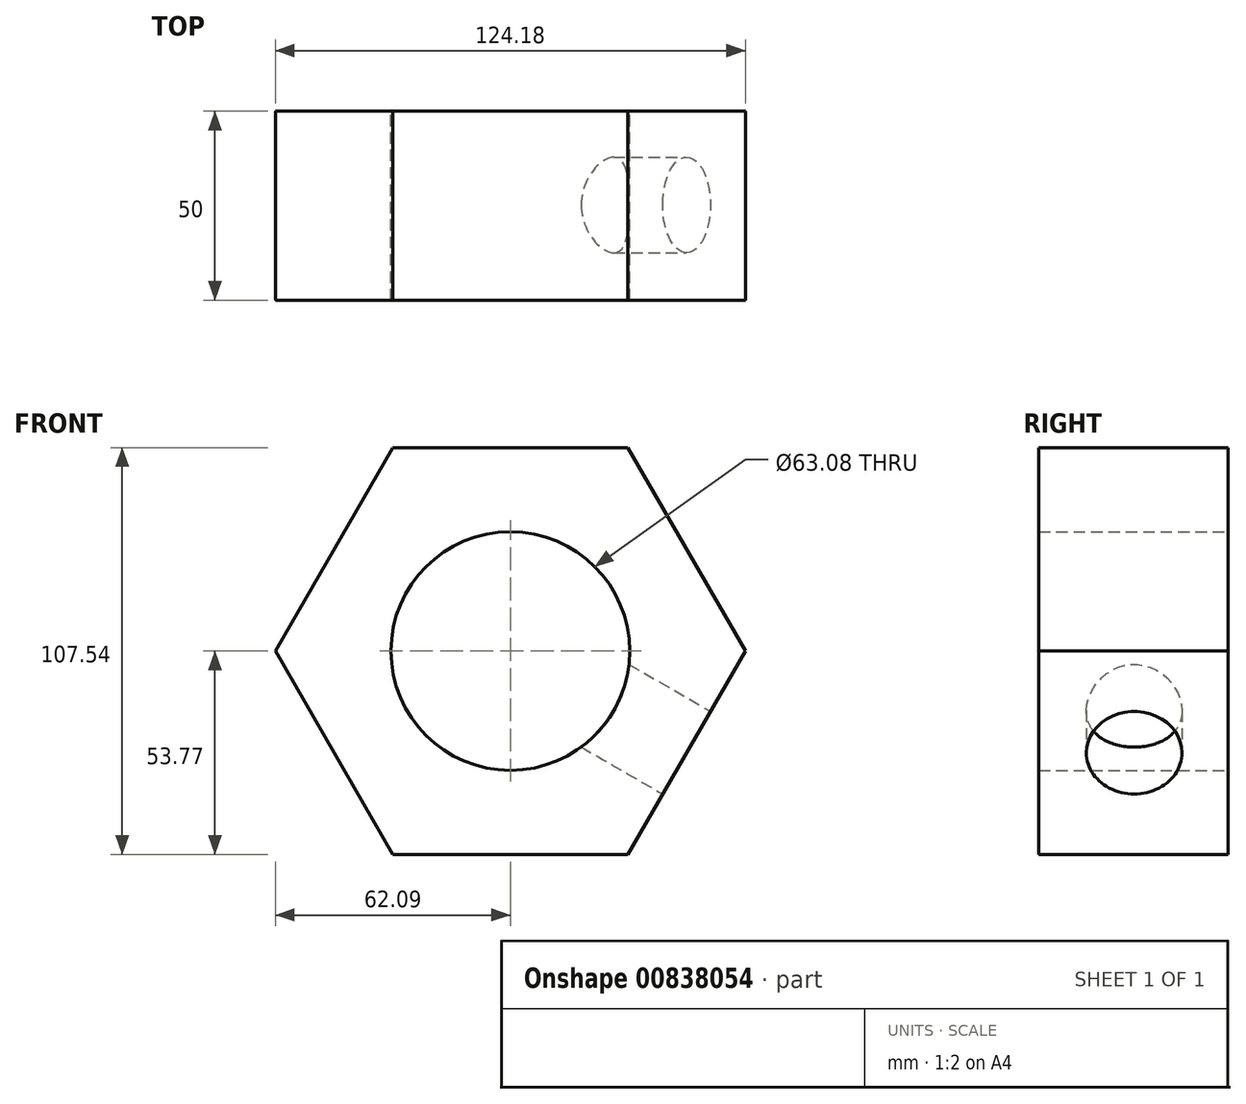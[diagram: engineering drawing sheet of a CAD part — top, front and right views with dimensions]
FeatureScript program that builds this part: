
annotation { "Feature Type Name" : "Feature", "Feature Type Description" : "" }
export const myFeature = defineFeature(function(context is Context, id is Id, definition is map)
    precondition{}
    {
        {
            var Q0;
            Q0=qCreatedBy(makeId("Front.planeOp"),FACE);
            var sketch = newSketch(context, id + "F0", { "sketchPlane" : qUnion([Q0])});
            skCircle(sketch, "E0.cCircle", {"center": v(0, 0) * mm, "radius": 62.09 * mm, "construction": true});
            skLineSegment(sketch, "E0.0", {"start": v(62.09, 0) * mm, "end": v(31.04, -53.77) * mm});
            skLineSegment(sketch, "E0.1", {"start": v(31.04, -53.77) * mm, "end": v(-31.04, -53.77) * mm});
            skLineSegment(sketch, "E0.2", {"start": v(-31.04, -53.77) * mm, "end": v(-62.09, 0) * mm});
            skLineSegment(sketch, "E0.3", {"start": v(-62.09, 0) * mm, "end": v(-31.04, 53.77) * mm});
            skLineSegment(sketch, "E0.4", {"start": v(-31.04, 53.77) * mm, "end": v(31.04, 53.77) * mm});
            skLineSegment(sketch, "E0.5", {"start": v(31.04, 53.77) * mm, "end": v(62.09, 0) * mm});
            skCircle(sketch, "E1", {"center": v(0, 0) * mm, "radius": 31.54 * mm});
            skSolve(sketch);
        }
        {
            var Q0;
            Q0=makeQuery(id+"F0.imprint","IMPRINT",FACE,{"disambiguationData":[TD([[makeQuery(id+"F0.imprint","IMPRINT",EDGE,{"derivedFrom":sQuery(id+"F0.wireOp",EDGE,"E0.0")}),-1.0]])]});
            extrude(context, id + "F1", {"entities" : qUnion([Q0]), "depth" : 50 * mm, "offsetDistance" : 25 * mm});
        }
        {
            var Q0;
            Q0=makeQuery(id+"F1.opExtrude","SWEPT_FACE",FACE,{"disambiguationData":[OSD([sQuery(id+"F0.wireOp",EDGE,"E0.0")])]});
            var sketch = newSketch(context, id + "F2", { "sketchPlane" : qUnion([Q0])});
            skCircle(sketch, "E2", {"center": v(-24.8, 0) * mm, "radius": 12.63 * mm});
            skSolve(sketch);
        }
        {
            var Q0;
            Q0=qSketchRegion(id+"F2",true);
            extrude(context, id + "F3", {"entities" : qUnion([Q0]), "operationType" : NewBodyOperationType.REMOVE, "oppositeDirection" : true, "depth" : 25 * mm, "offsetDistance" : 25 * mm});
        }
    });
